# Revit family: x290 Series Automatic
name_source: partatom
category: Mechanical Equipment
revit_build: Autodesk Revit 2014 (Build: 20130308_1515(x64)
units: mm (PartAtom-declared; Revit-internal decimal feet)

## types (9) — shared parameters
Assembly Code = D2010900
Cooling = Oil Filled
Cord Length = 240"
Cord Type = UL listed, 3-wire neoprene cord and plug (1 Ph) or 4-wire cord and plug
Default Elevation = 0"
Description = Single Seal Automatic Submersible Sewage or Dewatering Pumps
Discharge Diameter = 2" or 3" NPT
Discharge Height = 6"
Discharge Radius = 1"
Height = 19 5/16"
Hertz = 60
Impeller = Cast Iron
Impeller Type = Non-clogging vortex
Installation Type = Floor Mounted
Insulation = Class B
Lead Wires Insulation = Class B
Length = 12 7/8"
Manufacturer = Zoeller
Material = Cast Iron-Zoeller-Powder Coated Epoxy
Max. Operating Temp. = 130.00 °F
Mechanical Seals = Carbon and Ceramic
Motor Protection = Auto reset thermal overload
Motor Type = Submersible
Off Point = 5 1/4"
On Point = 15 3/4"
Operation = Automatic
Phase = 1 Ph
Price = Prices may vary. Please consult Manufacturer Representative for most up-to-date price list.
Product Page URL = http://www.zoellerpumps.com
RPM = 3450
Shipping Weight = 86-89 lbs
Solid Handling = 2" Spherical Solids
Square Ring & Gasket = Neoprene
Type = Permanent Split Capacitor
Type Comments = Available in single or double seal designs.
URL = http://www.zoellerpumps.com
Warranty Information = 18 Months (Limited)
Waste Connection = Yes
Width = 10 15/32"

## per-type parameters (varying)
| type | Amps | Apparent Load | Flow 292, 294, 295 @ 5', 293 @ 15' | Maximum Head | Minimum Head | Model | Motor | Voltage |
| 292-115V 1Ph | 15 A | 1725 VA | 140 GPM | 504" | Not Applicable | 292 | 1/2 HP | 115 V |
| 292-230V 1Ph | 8 A | 1725 VA | 140 GPM | 504" | Not Applicable | 292 | 1/2 HP | 230 V |
| 292-200V 1Ph | 9 A | 1760 VA | 140 GPM | 504" | Not Applicable | 292 | 1/2 HP | 200 V |
| 293-230V 1Ph | 10 A | 2346 VA | 118 GPM | 600" | 180" | 293 | 1/2 HP | 230 V |
| 293-200V 1Ph | 12 A | 2440 VA | 118 GPM | 600" | 180" | 293 | 1/2 HP | 200 V |
| 294-230V 1Ph | 14 A | 3151 VA | 196 GPM | 744" | Not Applicable | 294 | 1 1/2 HP | 230 V |
| 294-200V 1Ph | 18 A | 3560 VA | 196 GPM | 744" | Not Applicable | 294 | 1 1/2 HP | 200 V |
| 295-230V 1Ph | 17 A | 3933 VA | 214 GPM | 900" | Not Applicable | 295 | 2 HP | 230 V |
| 295-200V 1Ph | 21 A | 4100 VA | 214 GPM | 900" | Not Applicable | 295 | 2 HP | 200 V |

## geometry (parser evidence)
native form markers: Blend x6
no freeform markers — native parametric forms only
